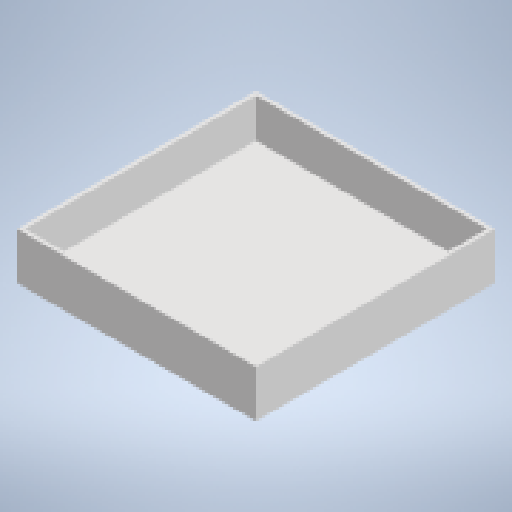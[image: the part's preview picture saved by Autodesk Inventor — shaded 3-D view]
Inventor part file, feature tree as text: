
AUTODESK INVENTOR PART (.ipt)
format: ipt  version: 2025.1 (Build 291241000, 241)  size: 232,448 bytes
history: native  units: mm
features: extrude x2, sketch x2, other x1
ambient origin geometry x8: Origin, YZ Plane, XZ Plane, XY Plane, X Axis, Y Axis, Z Axis, Center Point
bodies: Body1 (feature_tree)
feature tree (5):
  other  "Sólido1"
  extrude  "Extrusão1"  Depth=305.0mm
  extrude  "Extrusão2"  Depth=50.0mm
  sketch  "Esboço1"  dims[d0=305.0mm d1=305.0mm]
  sketch  "Esboço2"  dims[d2=152.5mm d3=152.5mm d8=60.0mm d9=0.0mm d10=5.0mm d11=5.0mm d12=5.0mm d13=5.0mm d14=50.0mm d15=0.0mm d4=0.5mm d5=0.872665mm d6=0.5mm d7=0.872665mm]
